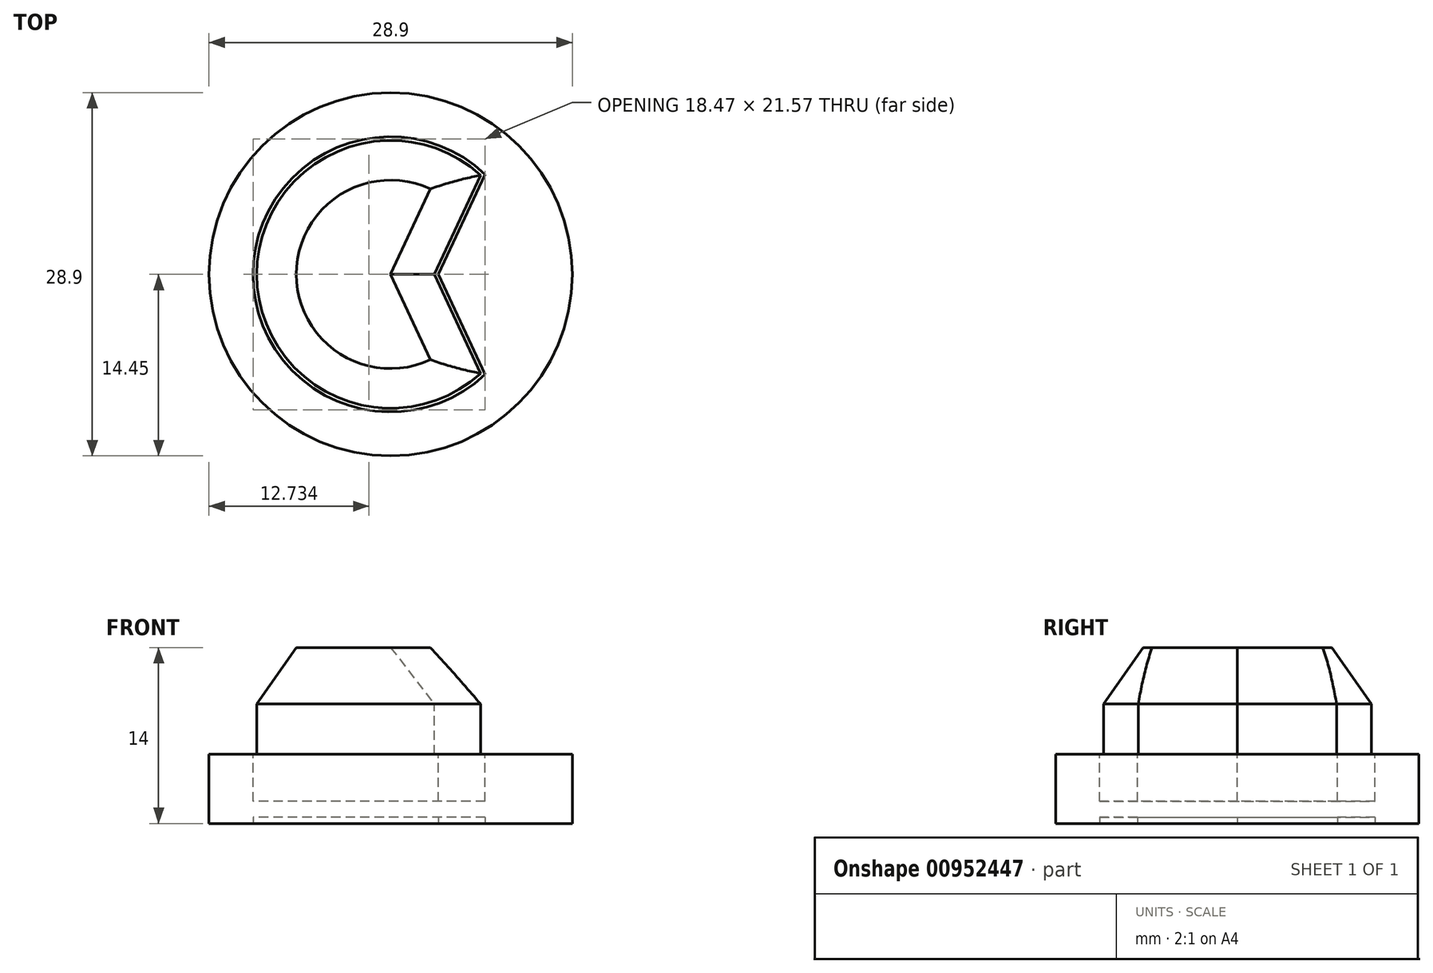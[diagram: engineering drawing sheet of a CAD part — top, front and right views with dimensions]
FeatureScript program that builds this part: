
annotation { "Feature Type Name" : "Feature", "Feature Type Description" : "" }
export const myFeature = defineFeature(function(context is Context, id is Id, definition is map)
    precondition{}
    {
        {
            var Q0;
            Q0=qCreatedBy(makeId("Top.planeOp"),FACE);
            var sketch = newSketch(context, id + "F0", { "sketchPlane" : qUnion([Q0])});
            skArc(sketch, "E0", {"start": v(3.17, 6.8) * mm, "mid": v(-7.5, 0) * mm, "end": v(3.17, -6.8) * mm});
            skLineSegment(sketch, "E1", {"start": v(0, 0) * mm, "end": v(3.17, -6.8) * mm});
            skLineSegment(sketch, "E2", {"start": v(0, 0) * mm, "end": v(3.17, 6.8) * mm});
            skSolve(sketch);
        }
        {
            var Q0;
            Q0=makeQuery(id+"F0.imprint","IMPRINT",FACE,{"disambiguationData":[TD([[makeQuery(id+"F0.imprint","IMPRINT",EDGE,{"derivedFrom":sQuery(id+"F0.wireOp",EDGE,"E0")}),1.0]])]});
            extrude(context, id + "F1", {"entities" : qUnion([Q0]), "oppositeDirection" : true, "depth" : 4.5 * mm, "offsetDistance" : 25 * mm, "hasDraft" : true, "draftAngle" : 35 * degree});
        }
        {
            var Q0;
            Q0=makeQuery(id+"F1.opExtrude","CAP_FACE",FACE,{"disambiguationData":[OSD([sQuery(id+"F0.wireOp",EDGE,"E0"),sQuery(id+"F0.wireOp",EDGE,"E1"),sQuery(id+"F0.wireOp",EDGE,"E2")])],"isStart":false});
            extrude(context, id + "F2", {"entities" : qUnion([Q0]), "operationType" : NewBodyOperationType.ADD, "depth" : 4 * mm, "offsetDistance" : 25 * mm});
        }
        {
            var Q0;
            Q0=makeQuery(id+"F2.opExtrude","CAP_FACE",FACE,{"disambiguationData":[OSD([sQuery(id+"F0.wireOp",EDGE,"E0"),sQuery(id+"F0.wireOp",EDGE,"E1"),sQuery(id+"F0.wireOp",EDGE,"E2")])],"isStart":false});
            var sketch = newSketch(context, id + "F3", { "sketchPlane" : qUnion([Q0])});
            skLineSegment(sketch, "E3.0", {"start": v(3.8, 0) * mm, "end": v(7.52, 7.96) * mm});
            skLineSegment(sketch, "E3.1", {"start": v(7.52, -7.96) * mm, "end": v(3.8, 0) * mm});
            skArc(sketch, "E3.2", {"start": v(7.52, 7.96) * mm, "mid": v(-10.95, 0) * mm, "end": v(7.52, -7.96) * mm});
            skCircle(sketch, "E4", {"center": v(0, 0) * mm, "radius": 14.45 * mm});
            skSolve(sketch);
        }
        {
            var Q0;
            Q0=makeQuery(id+"F3.imprint","IMPRINT",FACE,{"disambiguationData":[TD([[makeQuery(id+"F3.imprint","IMPRINT",EDGE,{"derivedFrom":sQuery(id+"F3.wireOp",EDGE,"E3.0")}),1.0]])]});
            var Q1;
            Q1=makeQuery(id+"F3.imprint","IMPRINT",FACE,{"disambiguationData":[TD([[makeQuery(id+"F3.imprint","IMPRINT",EDGE,{"derivedFrom":sQuery(id+"F3.wireOp",EDGE,"E3.0")}),-1.0]])]});
            var Q2;
            Q2=makeQuery(id+"F3.imprint","IMPRINT",FACE,{"disambiguationData":[TD([[makeQuery(id+"F3.imprint","IMPRINT",EDGE,{"derivedFrom":makeQuery(id+"F2.opExtrude","CAP_EDGE",EDGE,{"disambiguationData":[OSD([sQuery(id+"F0.wireOp",EDGE,"E0")])],"isStart":false})}),-1.0]])]});
            extrude(context, id + "F4", {"entities" : qUnion([Q0, Q1, Q2]), "depth" : 5.5 * mm, "offsetDistance" : 25 * mm});
        }
        {
            var Q0;
            Q0=makeQuery(id+"F3.imprint","IMPRINT",FACE,{"disambiguationData":[TD([[makeQuery(id+"F3.imprint","IMPRINT",EDGE,{"derivedFrom":sQuery(id+"F3.wireOp",EDGE,"E3.0")}),1.0]])]});
            var Q1;
            Q1=makeQuery(id+"F3.imprint","IMPRINT",FACE,{"disambiguationData":[TD([[makeQuery(id+"F3.imprint","IMPRINT",EDGE,{"derivedFrom":makeQuery(id+"F2.opExtrude","CAP_EDGE",EDGE,{"disambiguationData":[OSD([sQuery(id+"F0.wireOp",EDGE,"E0")])],"isStart":false})}),-1.0]])]});
            extrude(context, id + "F5", {"entities" : qUnion([Q0, Q1]), "operationType" : NewBodyOperationType.REMOVE, "depth" : 3.75 * mm, "offsetDistance" : 25 * mm});
        }
        {
            var Q0;
            Q0=makeQuery(id+"F4.opExtrude","CAP_FACE",FACE,{"disambiguationData":[OSD([sQuery(id+"F3.wireOp",EDGE,"E4")])],"isStart":false});
            var sketch = newSketch(context, id + "F6", { "sketchPlane" : qUnion([Q0])});
            skCircle(sketch, "E5", {"center": v(0, 0) * mm, "radius": 14.45 * mm});
            skCircle(sketch, "E6", {"center": v(0, 0) * mm, "radius": 10.95 * mm});
            skLineSegment(sketch, "E7", {"start": v(7.52, 7.96) * mm, "end": v(3.8, 0) * mm});
            skLineSegment(sketch, "E8", {"start": v(3.8, 0) * mm, "end": v(7.52, -7.96) * mm});
            skSolve(sketch);
        }
        {
            var Q0;
            {var subQ0=sQuery(id+"F6.wireOp",EDGE,"E7");Q0=makeQuery(id+"F6.imprint","IMPRINT",FACE,{"disambiguationData":[TD([[makeQuery(id+"F6.imprint","IMPRINT",EDGE,{"derivedFrom":subQ0}),-1.0]])]});}
            extrude(context, id + "F7", {"entities" : qUnion([Q0]), "operationType" : NewBodyOperationType.REMOVE, "oppositeDirection" : true, "depth" : .5 * mm, "offsetDistance" : 25 * mm});
        }
        {
            var Q0;
            Q0=makeQuery(id+"F3.imprint","IMPRINT",FACE,{"disambiguationData":[TD([[makeQuery(id+"F3.imprint","IMPRINT",EDGE,{"derivedFrom":sQuery(id+"F3.wireOp",EDGE,"E3.0")}),1.0]])]});
            var Q1;
            Q1=makeQuery(id+"F3.imprint","IMPRINT",FACE,{"disambiguationData":[TD([[makeQuery(id+"F3.imprint","IMPRINT",EDGE,{"derivedFrom":makeQuery(id+"F2.opExtrude","CAP_EDGE",EDGE,{"disambiguationData":[OSD([sQuery(id+"F0.wireOp",EDGE,"E0")])],"isStart":false})}),-1.0]])]});
            extrude(context, id + "F8", {"entities" : qUnion([Q0, Q1]), "operationType" : NewBodyOperationType.REMOVE, "depth" : 3.75 * mm, "offsetDistance" : 25 * mm});
        }
    });
